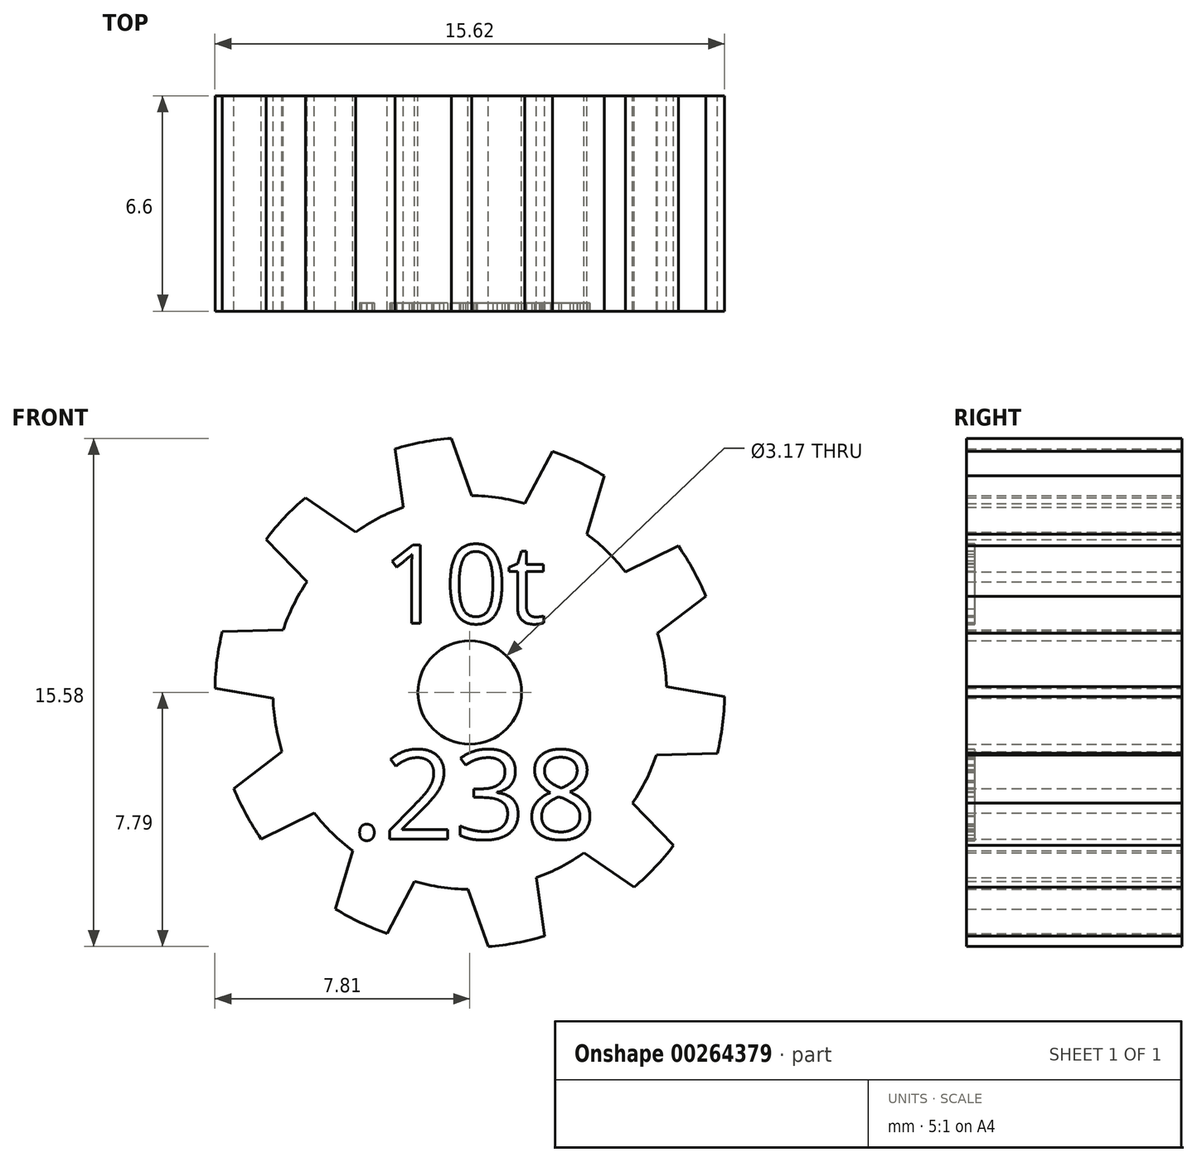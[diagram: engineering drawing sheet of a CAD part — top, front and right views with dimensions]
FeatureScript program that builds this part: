
annotation { "Feature Type Name" : "Feature", "Feature Type Description" : "" }
export const myFeature = defineFeature(function(context is Context, id is Id, definition is map)
    precondition{}
    {
        {
            var Q0;
            Q0=qCreatedBy(makeId("Front.planeOp"),FACE);
            var sketch = newSketch(context, id + "F0", { "sketchPlane" : qUnion([Q0])});
            skCircle(sketch, "E0", {"center": v(0, 0) * mm, "radius": 6.03 * mm});
            skCircle(sketch, "E1", {"center": v(0, 0) * mm, "radius": 1.59 * mm});
            skSolve(sketch);
        }
        {
            var Q0;
            Q0=qSketchRegion(id+"F0",true);
            extrude(context, id + "F1", {"entities" : qUnion([Q0]), "depth" : 6.6 * mm});
        }
        {
            var Q0;
            Q0=makeQuery(id+"F1.opExtrude","CAP_FACE",FACE,{"disambiguationData":[OSD([sQuery(id+"F0.wireOp",EDGE,"E0"),sQuery(id+"F0.wireOp",EDGE,"E1")])],"isStart":false});
            var sketch = newSketch(context, id + "F2", { "sketchPlane" : qUnion([Q0])});
            skText(sketch, "E2", { "text": "10t\n", "fontName": "OpenSans-Regular.ttf"});
            skText(sketch, "E3", { "text": ".238", "fontName": "OpenSans-Regular.ttf"});
            const initialGuessF2  = {"E2": [-0.00269, 0.00212, 1, 0, 0.00242], "E3": [-0.00366, -0.00449, 1, 0, 0.00274]};
            skSetInitialGuess(sketch, initialGuessF2);
            skSolve(sketch);
        }
        {
            var Q0;
            Q0=qSketchRegion(id+"F2",true);
            extrude(context, id + "F3", {"entities" : qUnion([Q0]), "operationType" : NewBodyOperationType.REMOVE, "oppositeDirection" : true, "depth" : 0.25 * mm});
        }
        {
            var Q0;
            Q0=qCreatedBy(makeId("Front.planeOp"),FACE);
            var sketch = newSketch(context, id + "F4", { "sketchPlane" : qUnion([Q0])});
            skLineSegment(sketch, "E4", {"start": v(0, 0) * mm, "end": v(0, 8.24) * mm, "construction": true});
            skLineSegment(sketch, "E5", {"start": v(0, 0) * mm, "end": v(-5.25, 7.22) * mm, "construction": true});
            skLineSegment(sketch, "E6", {"start": v(0, 0) * mm, "end": v(-2.49, 7.66) * mm, "construction": true});
            skArc(sketch, "E7.0", {"start": v(-0.57, 7.79) * mm, "mid": v(-1.44, 7.68) * mm, "end": v(-2.3, 7.47) * mm});
            skLineSegment(sketch, "E8", {"start": v(0.08, 5.97) * mm, "end": v(-0.57, 7.79) * mm});
            skLineSegment(sketch, "E9", {"start": v(-2.3, 7.47) * mm, "end": v(-2.01, 5.52) * mm});
            skLineSegment(sketch, "E10", {"start": v(-2.01, 5.52) * mm, "end": v(0.08, 5.97) * mm});
            skArc(sketch, "E11.1.0", {"start": v(-5.04, 5.97) * mm, "mid": v(-5.68, 5.36) * mm, "end": v(-6.24, 4.7) * mm});
            skLineSegment(sketch, "E11.1.1", {"start": v(-3.45, 4.87) * mm, "end": v(-5.04, 5.97) * mm});
            skLineSegment(sketch, "E11.1.2", {"start": v(-4.88, 3.28) * mm, "end": v(-3.45, 4.87) * mm});
            skLineSegment(sketch, "E11.1.3", {"start": v(-6.24, 4.7) * mm, "end": v(-4.88, 3.28) * mm});
            skArc(sketch, "E11.2.0", {"start": v(-7.58, 1.87) * mm, "mid": v(-7.75, 1) * mm, "end": v(-7.8, 0.12) * mm});
            skLineSegment(sketch, "E11.2.1", {"start": v(-5.65, 1.92) * mm, "end": v(-7.58, 1.87) * mm});
            skLineSegment(sketch, "E11.2.2", {"start": v(-5.87, -0.2) * mm, "end": v(-5.65, 1.92) * mm});
            skLineSegment(sketch, "E11.2.3", {"start": v(-7.8, 0.12) * mm, "end": v(-5.87, -0.2) * mm});
            skArc(sketch, "E11.3.0", {"start": v(-7.23, -2.95) * mm, "mid": v(-6.86, -3.74) * mm, "end": v(-6.4, -4.49) * mm});
            skLineSegment(sketch, "E11.3.1", {"start": v(-5.7, -1.77) * mm, "end": v(-7.23, -2.95) * mm});
            skLineSegment(sketch, "E11.3.2", {"start": v(-4.63, -3.62) * mm, "end": v(-5.7, -1.77) * mm});
            skLineSegment(sketch, "E11.3.3", {"start": v(-6.4, -4.49) * mm, "end": v(-4.63, -3.62) * mm});
            skArc(sketch, "E11.4.0", {"start": v(-4.12, -6.64) * mm, "mid": v(-3.35, -7.06) * mm, "end": v(-2.53, -7.39) * mm});
            skLineSegment(sketch, "E11.4.1", {"start": v(-3.57, -4.78) * mm, "end": v(-4.12, -6.64) * mm});
            skLineSegment(sketch, "E11.4.2", {"start": v(-1.62, -5.65) * mm, "end": v(-3.57, -4.78) * mm});
            skLineSegment(sketch, "E11.4.3", {"start": v(-2.53, -7.39) * mm, "end": v(-1.62, -5.65) * mm});
            skArc(sketch, "E11.5.0", {"start": v(0.57, -7.79) * mm, "mid": v(1.44, -7.68) * mm, "end": v(2.3, -7.47) * mm});
            skLineSegment(sketch, "E11.5.1", {"start": v(-0.08, -5.97) * mm, "end": v(0.57, -7.79) * mm});
            skLineSegment(sketch, "E11.5.2", {"start": v(2.01, -5.52) * mm, "end": v(-0.08, -5.97) * mm});
            skLineSegment(sketch, "E11.5.3", {"start": v(2.3, -7.47) * mm, "end": v(2.01, -5.52) * mm});
            skArc(sketch, "E11.6.0", {"start": v(5.04, -5.97) * mm, "mid": v(5.68, -5.36) * mm, "end": v(6.24, -4.7) * mm});
            skLineSegment(sketch, "E11.6.1", {"start": v(3.45, -4.87) * mm, "end": v(5.04, -5.97) * mm});
            skLineSegment(sketch, "E11.6.2", {"start": v(4.88, -3.28) * mm, "end": v(3.45, -4.87) * mm});
            skLineSegment(sketch, "E11.6.3", {"start": v(6.24, -4.7) * mm, "end": v(4.88, -3.28) * mm});
            skArc(sketch, "E11.7.0", {"start": v(7.58, -1.87) * mm, "mid": v(7.75, -1) * mm, "end": v(7.8, -0.12) * mm});
            skLineSegment(sketch, "E11.7.1", {"start": v(5.65, -1.92) * mm, "end": v(7.58, -1.87) * mm});
            skLineSegment(sketch, "E11.7.2", {"start": v(5.87, 0.2) * mm, "end": v(5.65, -1.92) * mm});
            skLineSegment(sketch, "E11.7.3", {"start": v(7.8, -0.12) * mm, "end": v(5.87, 0.2) * mm});
            skArc(sketch, "E11.8.0", {"start": v(7.23, 2.95) * mm, "mid": v(6.86, 3.74) * mm, "end": v(6.4, 4.49) * mm});
            skLineSegment(sketch, "E11.8.1", {"start": v(5.7, 1.77) * mm, "end": v(7.23, 2.95) * mm});
            skLineSegment(sketch, "E11.8.2", {"start": v(4.63, 3.62) * mm, "end": v(5.7, 1.77) * mm});
            skLineSegment(sketch, "E11.8.3", {"start": v(6.4, 4.49) * mm, "end": v(4.63, 3.62) * mm});
            skArc(sketch, "E11.9.0", {"start": v(4.12, 6.64) * mm, "mid": v(3.35, 7.06) * mm, "end": v(2.53, 7.39) * mm});
            skLineSegment(sketch, "E11.9.1", {"start": v(3.57, 4.78) * mm, "end": v(4.12, 6.64) * mm});
            skLineSegment(sketch, "E11.9.2", {"start": v(1.62, 5.65) * mm, "end": v(3.57, 4.78) * mm});
            skLineSegment(sketch, "E11.9.3", {"start": v(2.53, 7.39) * mm, "end": v(1.62, 5.65) * mm});
            skSolve(sketch);
        }
        {
            var Q0;
            Q0=qSketchRegion(id+"F4",true);
            var Q1;
            {var subQ0=sQuery(id+"F0.wireOp",EDGE,"E0");var subQ1=sQuery(id+"F0.wireOp",EDGE,"E1");Q1=makeQuery(id+"F3.boolean.opBoolean","SPLIT",FACE,{"disambiguationData":[TD([makeQuery(id+"F1.opExtrude","SWEPT_FACE",FACE,{"disambiguationData":[OSD([subQ0])]})])],"derivedFrom":makeQuery(id+"F1.opExtrude","CAP_FACE",FACE,{"disambiguationData":[OSD([subQ0,subQ1])],"isStart":false})});}
            extrude(context, id + "F5", {"entities" : qUnion([Q0]), "operationType" : NewBodyOperationType.ADD, "endBound" : BoundingType.UP_TO_SURFACE, "endBoundEntityFace" : qUnion([Q1]), "depth" : 25.4 * mm});
        }
    });
